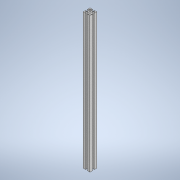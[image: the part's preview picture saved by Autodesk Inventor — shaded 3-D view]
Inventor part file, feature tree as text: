
AUTODESK INVENTOR PART (.ipt)
format: ipt  version: 2022 (Build 260153000, 153)  size: 156,672 bytes
history: native  units: in
note: dims shown in document units (in); Inventor stores cm internally (conversion verified against a paired STEP export)
features: sketch x2, extrude x1, hole x1
ambient origin geometry x8: Origin, YZ Plane, XZ Plane, XY Plane, X Axis, Y Axis, Z Axis, Center Point
bodies: Body1 (feature_tree)
feature tree (4):
  extrude  "Extrusion1"  [1 undecoded]
  hole  "Hole1"  [1 undecoded]
  sketch  "Sketch1"  dims[d0=15.748in d1=0.0in]
  sketch  "Sketch2"  dims[d2=0.1575in d3=0.2362in d4=0.1575in d5=0.0787in d6=90.0deg d7=0.315in d8=0.8108in]
note: 2 required parameter values undecoded (feature->parameter linkage not recoverable at this tier; creation-order binding heuristic only, values carry confidence <= 0.55)
